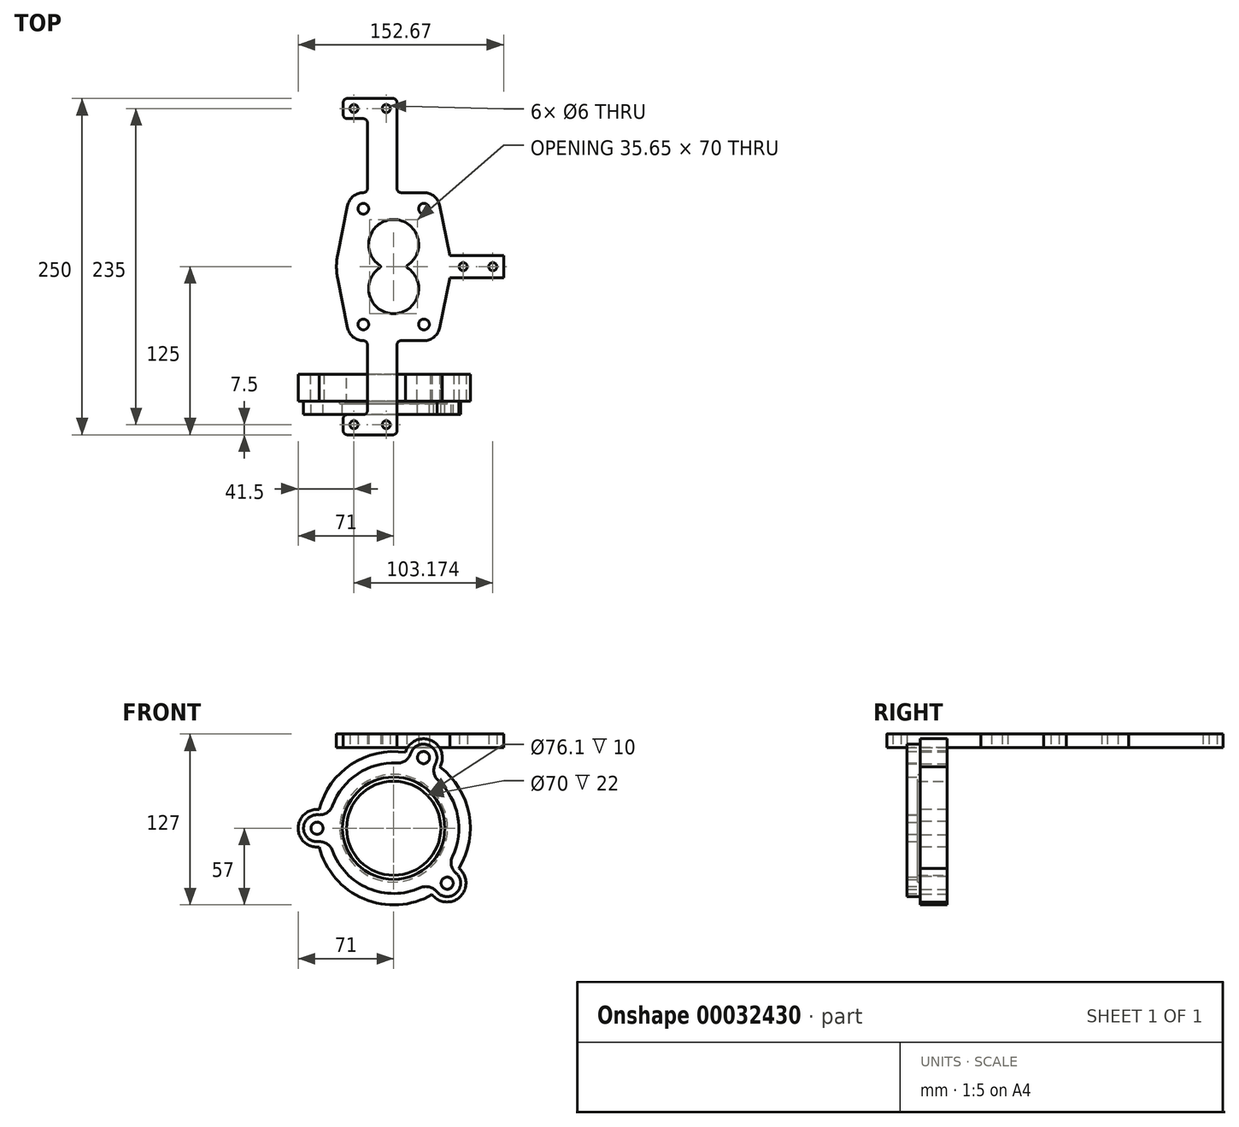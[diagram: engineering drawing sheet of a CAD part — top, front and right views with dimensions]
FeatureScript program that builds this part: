
annotation { "Feature Type Name" : "Feature", "Feature Type Description" : "" }
export const myFeature = defineFeature(function(context is Context, id is Id, definition is map)
    precondition{}
    {
        {
            var Q0;
            Q0=qCreatedBy(makeId("Front.planeOp"),FACE);
            var sketch = newSketch(context, id + "F0", { "sketchPlane" : qUnion([Q0])});
            skCircle(sketch, "E0", {"center": v(0, 0) * mm, "radius": 35 * mm});
            skCircle(sketch, "E1", {"center": v(0, 0) * mm, "radius": 40 * mm, "construction": true});
            skLineSegment(sketch, "E2", {"start": v(22.17, 52.51) * mm, "end": v(-57, 0) * mm, "construction": true});
            skLineSegment(sketch, "E3", {"start": v(39.76, -40.84) * mm, "end": v(22.17, 52.51) * mm, "construction": true});
            skLineSegment(sketch, "E4", {"start": v(-57, 0) * mm, "end": v(39.76, -40.84) * mm, "construction": true});
            skCircle(sketch, "E5", {"center": v(39.76, -40.84) * mm, "radius": 5 * mm});
            skCircle(sketch, "E6", {"center": v(22.17, 52.51) * mm, "radius": 5 * mm});
            skCircle(sketch, "E7", {"center": v(-57, 0) * mm, "radius": 5 * mm});
            skArc(sketch, "E8", {"start": v(34.3, 45.53) * mm, "mid": v(27.61, 65.41) * mm, "end": v(8.7, 56.33) * mm});
            skArc(sketch, "E9", {"start": v(28.6, -49.3) * mm, "mid": v(49.52, -50.88) * mm, "end": v(48.52, -29.92) * mm});
            skArc(sketch, "E10", {"start": v(-55.28, 13.9) * mm, "mid": v(-71, 0) * mm, "end": v(-55.28, -13.9) * mm});
            skArc(sketch, "E11.trimOffspring", {"start": v(8.7, 56.33) * mm, "mid": v(-31.5, 47.5) * mm, "end": v(-55.28, 13.9) * mm});
            skArc(sketch, "E12.trimOffspring", {"start": v(48.52, -29.92) * mm, "mid": v(56.01, 10.56) * mm, "end": v(34.3, 45.53) * mm});
            skArc(sketch, "E13.trimOffspring", {"start": v(-55.28, -13.9) * mm, "mid": v(-22.17, -52.51) * mm, "end": v(28.6, -49.3) * mm});
            skCircle(sketch, "E14", {"center": v(0, 0) * mm, "radius": 57 * mm, "construction": true});
            skSolve(sketch);
        }
        {
            var Q0;
            Q0=qCreatedBy(makeId("Top.planeOp"),FACE);
            cPlane(context, id + "F1", {"entities" : qUnion([Q0]), "cplaneType" : CPlaneType.OFFSET, "offset" : 60 * mm, "width" : 150 * mm, "height" : 150 * mm});
        }
        {
            var Q0;
            Q0=qCreatedBy(id+"F1.planeOp",FACE);
            var sketch = newSketch(context, id + "F2", { "sketchPlane" : qUnion([Q0])});
            skLineSegment(sketch, "E15.rect.bottom", {"start": v(22.5, 143) * mm, "end": v(-22.5, 143) * mm, "construction": true});
            skLineSegment(sketch, "E15.rect.top", {"start": v(22.5, 57) * mm, "end": v(-22.5, 57) * mm, "construction": true});
            skLineSegment(sketch, "E15.rect.left", {"start": v(22.5, 143) * mm, "end": v(22.5, 57) * mm, "construction": true});
            skLineSegment(sketch, "E15.rect.right", {"start": v(-22.5, 143) * mm, "end": v(-22.5, 57) * mm, "construction": true});
            skPoint(sketch, "E15.rect.middle", {"position": v(0, 100) * mm});
            skCircle(sketch, "E16", {"center": v(-22.5, 143) * mm, "radius": 4 * mm});
            skCircle(sketch, "E17", {"center": v(22.5, 143) * mm, "radius": 4 * mm});
            skCircle(sketch, "E18", {"center": v(22.5, 57) * mm, "radius": 4 * mm});
            skCircle(sketch, "E19", {"center": v(-22.5, 57) * mm, "radius": 4 * mm});
            skArc(sketch, "E20", {"start": v(-41.67, 108.34) * mm, "mid": v(-42.5, 100) * mm, "end": v(-41.67, 91.66) * mm});
            skArc(sketch, "E21", {"start": v(-22.5, 155) * mm, "mid": v(-30.1, 152.28) * mm, "end": v(-34.27, 145.35) * mm});
            skLineSegment(sketch, "E22", {"start": v(-34.27, 54.65) * mm, "end": v(-41.67, 91.66) * mm});
            skLineSegment(sketch, "E23", {"start": v(-34.27, 145.35) * mm, "end": v(-41.67, 108.34) * mm});
            skLineSegment(sketch, "E24", {"start": v(0, 155) * mm, "end": v(0, 45) * mm, "construction": true});
            skLineSegment(sketch, "E25", {"start": v(0, 45) * mm, "end": v(-22.5, 45) * mm, "construction": true});
            skArc(sketch, "E26.trimOffspring", {"start": v(-34.27, 54.65) * mm, "mid": v(-30.1, 47.72) * mm, "end": v(-22.5, 45) * mm});
            skLineSegment(sketch, "E27.MirrorCS", {"start": v(5.5, 155) * mm, "end": v(22.5, 155) * mm});
            skArc(sketch, "E28.MirrorCS", {"start": v(22.5, 155) * mm, "mid": v(30.1, 152.28) * mm, "end": v(34.27, 145.35) * mm});
            skLineSegment(sketch, "E29.MirrorCS", {"start": v(34.27, 145.35) * mm, "end": v(41.67, 108.34) * mm});
            skArc(sketch, "E30.MirrorCS", {"start": v(41.67, 108.34) * mm, "mid": v(42.5, 100) * mm, "end": v(41.67, 91.66) * mm, "construction": true});
            skLineSegment(sketch, "E31.MirrorCS", {"start": v(34.27, 54.65) * mm, "end": v(41.67, 91.66) * mm});
            skArc(sketch, "E32.MirrorCS", {"start": v(34.27, 54.65) * mm, "mid": v(30.1, 47.72) * mm, "end": v(22.5, 45) * mm});
            skLineSegment(sketch, "E33.MirrorCS", {"start": v(5.5, 45) * mm, "end": v(22.5, 45) * mm});
            skPoint(sketch, "E34.rect.bottom.start.orphan", {"position": v(0, 155) * mm});
            skLineSegment(sketch, "E35", {"start": v(41.67, 108.34) * mm, "end": v(81.67, 108.34) * mm});
            skLineSegment(sketch, "E36", {"start": v(81.67, 108.34) * mm, "end": v(81.67, 91.66) * mm});
            skLineSegment(sketch, "E37", {"start": v(81.67, 91.66) * mm, "end": v(41.67, 91.66) * mm});
            skArc(sketch, "E38.filletArc", {"start": v(-22.5, 155) * mm, "mid": v(-20.38, 155.88) * mm, "end": v(-19.5, 158) * mm});
            skArc(sketch, "E39.filletArc", {"start": v(2.5, 158) * mm, "mid": v(3.38, 155.88) * mm, "end": v(5.5, 155) * mm});
            skLineSegment(sketch, "E40", {"start": v(-19.5, 158) * mm, "end": v(-19.5, 207) * mm});
            skLineSegment(sketch, "E41", {"start": v(-22.5, 210) * mm, "end": v(-34.5, 210) * mm});
            skLineSegment(sketch, "E42", {"start": v(-37.5, 213) * mm, "end": v(-37.5, 222) * mm});
            skLineSegment(sketch, "E43", {"start": v(-34.5, 225) * mm, "end": v(-0.5, 225) * mm});
            skLineSegment(sketch, "E44", {"start": v(2.5, 222) * mm, "end": v(2.5, 158) * mm});
            skCircle(sketch, "E45", {"center": v(-29.5, 217.5) * mm, "radius": 3 * mm});
            skCircle(sketch, "E46", {"center": v(-5.5, 217.5) * mm, "radius": 3 * mm});
            skLineSegment(sketch, "E47", {"start": v(-29.5, 217.5) * mm, "end": v(-5.5, 217.5) * mm, "construction": true});
            skPoint(sketch, "E48.visualSharp", {"position": v(-37.5, 225) * mm});
            skArc(sketch, "E48.filletArc", {"start": v(-34.5, 225) * mm, "mid": v(-36.62, 224.12) * mm, "end": v(-37.5, 222) * mm});
            skPoint(sketch, "E49.visualSharp", {"position": v(2.5, 225) * mm});
            skArc(sketch, "E49.filletArc", {"start": v(2.5, 222) * mm, "mid": v(1.62, 224.12) * mm, "end": v(-0.5, 225) * mm});
            skPoint(sketch, "E50.visualSharp", {"position": v(-19.5, 210) * mm});
            skArc(sketch, "E50.filletArc", {"start": v(-19.5, 207) * mm, "mid": v(-20.38, 209.12) * mm, "end": v(-22.5, 210) * mm});
            skPoint(sketch, "E51.visualSharp", {"position": v(-37.5, 210) * mm});
            skArc(sketch, "E51.filletArc", {"start": v(-37.5, 213) * mm, "mid": v(-36.62, 210.88) * mm, "end": v(-34.5, 210) * mm});
            skLineSegment(sketch, "E52", {"start": v(0, 100) * mm, "end": v(-77.55, 100) * mm, "construction": true});
            skLineSegment(sketch, "E53", {"start": v(81.67, 100) * mm, "end": v(51.67, 100) * mm, "construction": true});
            skCircle(sketch, "E54", {"center": v(51.67, 100) * mm, "radius": 3 * mm});
            skCircle(sketch, "E55", {"center": v(73.67, 100) * mm, "radius": 3 * mm});
            skArc(sketch, "E56.MirrorCS", {"start": v(-37.5, -13) * mm, "mid": v(-36.62, -10.88) * mm, "end": v(-34.5, -10) * mm});
            skArc(sketch, "E57.MirrorCS", {"start": v(2.5, -22) * mm, "mid": v(1.62, -24.12) * mm, "end": v(-0.5, -25) * mm});
            skArc(sketch, "E58.MirrorCS", {"start": v(-19.5, -7) * mm, "mid": v(-20.38, -9.12) * mm, "end": v(-22.5, -10) * mm});
            skArc(sketch, "E59.MirrorCS", {"start": v(-34.5, -25) * mm, "mid": v(-36.62, -24.12) * mm, "end": v(-37.5, -22) * mm});
            skPoint(sketch, "E60.MirrorP", {"position": v(-37.5, -25) * mm});
            skLineSegment(sketch, "E61.MirrorCS", {"start": v(-29.5, -17.5) * mm, "end": v(-5.5, -17.5) * mm});
            skLineSegment(sketch, "E62.MirrorCS", {"start": v(-22.5, -10) * mm, "end": v(-34.5, -10) * mm});
            skPoint(sketch, "E63.MirrorP", {"position": v(-19.5, -10) * mm});
            skLineSegment(sketch, "E64.MirrorCS", {"start": v(2.5, -22) * mm, "end": v(2.5, 42) * mm});
            skPoint(sketch, "E65.MirrorP", {"position": v(2.5, -25) * mm});
            skCircle(sketch, "E66.MirrorC", {"center": v(-29.5, -17.5) * mm, "radius": 3 * mm});
            skPoint(sketch, "E67.MirrorP", {"position": v(-37.5, -10) * mm});
            skLineSegment(sketch, "E68.MirrorCS", {"start": v(-37.5, -13) * mm, "end": v(-37.5, -22) * mm});
            skLineSegment(sketch, "E69.MirrorCS", {"start": v(-19.5, 42) * mm, "end": v(-19.5, -7) * mm});
            skLineSegment(sketch, "E70.MirrorCS", {"start": v(-34.5, -25) * mm, "end": v(-0.5, -25) * mm});
            skCircle(sketch, "E71.MirrorC", {"center": v(-5.5, -17.5) * mm, "radius": 3 * mm});
            skArc(sketch, "E72.MirrorCS", {"start": v(-22.5, 45) * mm, "mid": v(-20.38, 44.12) * mm, "end": v(-19.5, 42) * mm});
            skArc(sketch, "E73.MirrorCS", {"start": v(2.5, 42) * mm, "mid": v(3.38, 44.12) * mm, "end": v(5.5, 45) * mm});
            skPoint(sketch, "E74.orphan", {"position": v(0, 45) * mm});
            skArc(sketch, "E75", {"start": v(-8.77, 100) * mm, "mid": v(0, 65) * mm, "end": v(8.77, 100) * mm});
            skLineSegment(sketch, "E76", {"start": v(0, 100) * mm, "end": v(0, 100) * mm});
            skCircle(sketch, "E77", {"center": v(0, 100) * mm, "radius": 35 * mm, "construction": true});
            skPoint(sketch, "E78", {"position": v(22.5, 100) * mm});
            skArc(sketch, "E79.converted", {"start": v(8.77, 100) * mm, "mid": v(0, 135) * mm, "end": v(-8.77, 100) * mm});
            skSolve(sketch);
        }
        {
            var Q0;
            Q0=qCreatedBy(makeId("Right.planeOp"),FACE);
            var sketch = newSketch(context, id + "F3", { "sketchPlane" : qUnion([Q0])});
            skLineSegment(sketch, "E80", {"start": v(0, 0) * mm, "end": v(19.92, 0) * mm});
            skSolve(sketch);
        }
        {
            var Q0;
            Q0=sQuery(id+"F3.wireOp",EDGE,"E80");
            cPlane(context, id + "F4", {"entities" : qUnion([Q0]), "cplaneType" : CPlaneType.LINE_ANGLE, "offset" : 150 * mm, "angle" : 65 * degree, "width" : 150 * mm, "height" : 150 * mm});
        }
        {
            var Q0;
            Q0=qCreatedBy(id+"F4.planeOp",FACE);
            var sketch = newSketch(context, id + "F5", { "sketchPlane" : qUnion([Q0])});
            skLineSegment(sketch, "E81", {"start": v(35.53, 0) * mm, "end": v(0, 0) * mm, "construction": true});
            skArc(sketch, "E82", {"start": v(0, 0) * mm, "mid": v(-23.3, -3.07) * mm, "end": v(-45, -12.06) * mm});
            skLineSegment(sketch, "E83", {"start": v(-45, -12.06) * mm, "end": v(0, -90) * mm, "construction": true});
            skLineSegment(sketch, "E84", {"start": v(0, 0) * mm, "end": v(0, -90) * mm, "construction": true});
            skSolve(sketch);
        }
        {
            var Q0;
            Q0=makeQuery(id+"F0.imprint","IMPRINT",FACE,{"disambiguationData":[TD([[makeQuery(id+"F0.imprint","IMPRINT",EDGE,{"derivedFrom":sQuery(id+"F0.wireOp",EDGE,"E0")}),-1.0]])]});
            var sketch = newSketch(context, id + "F6", { "sketchPlane" : qUnion([Q0])});
            skCircle(sketch, "E85", {"center": v(0, 0) * mm, "radius": 40 * mm});
            skSolve(sketch);
        }
        {
            var Q0;
            Q0=makeQuery(id+"F6.imprint","IMPRINT",FACE,{"disambiguationData":[TD([[makeQuery(id+"F6.imprint","IMPRINT",EDGE,{"derivedFrom":sQuery(id+"F6.wireOp",EDGE,"E85")}),1.0]])]});
            extrude(context, id + "F7", {"entities" : qUnion([Q0]), "depth" : 2 * mm});
        }
        {
            var Q0;
            Q0=makeQuery(id+"F0.imprint","IMPRINT",FACE,{"disambiguationData":[TD([[makeQuery(id+"F0.imprint","IMPRINT",EDGE,{"derivedFrom":sQuery(id+"F0.wireOp",EDGE,"E0")}),-1.0]])]});
            extrude(context, id + "F8", {"entities" : qUnion([Q0]), "operationType" : NewBodyOperationType.ADD, "oppositeDirection" : true, "depth" : 20 * mm});
        }
        {
            var Q0;
            Q0 = qSketchRegion(id + "F2", true);
            extrude(context, id + "F9", {"entities" : qUnion([Q0]), "depth" : 10 * mm});
        }
        {
            var Q0;
            Q0=makeQuery(id+"F8.opExtrude","CAP_FACE",FACE,{"disambiguationData":[OSD([sQuery(id+"F0.wireOp",EDGE,"E0"),sQuery(id+"F0.wireOp",EDGE,"E5"),sQuery(id+"F0.wireOp",EDGE,"E6"),sQuery(id+"F0.wireOp",EDGE,"E7"),sQuery(id+"F0.wireOp",EDGE,"E8"),sQuery(id+"F0.wireOp",EDGE,"E9"),sQuery(id+"F0.wireOp",EDGE,"E10"),sQuery(id+"F0.wireOp",EDGE,"E11.trimOffspring"),sQuery(id+"F0.wireOp",EDGE,"E12.trimOffspring"),sQuery(id+"F0.wireOp",EDGE,"E13.trimOffspring")])],"isStart":true});
            var sketch = newSketch(context, id + "F10", { "sketchPlane" : qUnion([Q0])});
            skCircle(sketch, "E86.0", {"center": v(39.76, -40.84) * mm, "radius": 4.5 * mm});
            skCircle(sketch, "E86.1", {"center": v(22.17, 52.51) * mm, "radius": 4.5 * mm});
            skCircle(sketch, "E86.2", {"center": v(-57, 0) * mm, "radius": 4.5 * mm});
            skCircle(sketch, "E87.0", {"center": v(0, 0) * mm, "radius": 38.05 * mm});
            skArc(sketch, "E88", {"start": v(43.72, -21) * mm, "mid": v(47.66, 8.98) * mm, "end": v(33.08, 35.47) * mm});
            skCircle(sketch, "E89", {"center": v(0, 0) * mm, "radius": 57 * mm, "construction": true});
            skArc(sketch, "E90", {"start": v(32, -47.16) * mm, "mid": v(46.73, -48) * mm, "end": v(46.29, -33.27) * mm});
            skLineSegment(sketch, "E91", {"start": v(32, -47.16) * mm, "end": v(19.81, -44.27) * mm, "construction": true});
            skLineSegment(sketch, "E92", {"start": v(46.29, -33.27) * mm, "end": v(43.72, -21) * mm, "construction": true});
            skLineSegment(sketch, "E93", {"start": v(0, 0) * mm, "end": v(39.76, -40.84) * mm, "construction": true});
            skLineSegment(sketch, "E94", {"start": v(0, 0) * mm, "end": v(-57, 0) * mm, "construction": true});
            skLineSegment(sketch, "E95", {"start": v(0, 0) * mm, "end": v(22.17, 52.51) * mm, "construction": true});
            skArc(sketch, "E96", {"start": v(43.72, -21) * mm, "mid": v(42.92, -27.57) * mm, "end": v(46.29, -33.27) * mm});
            skArc(sketch, "E97", {"start": v(32, -47.16) * mm, "mid": v(26.4, -43.65) * mm, "end": v(19.81, -44.27) * mm});
            skArc(sketch, "E98", {"start": v(-56.12, 9.96) * mm, "mid": v(-67, 0) * mm, "end": v(-56.12, -9.96) * mm});
            skArc(sketch, "E99.trimOffspring", {"start": v(-45.54, -16.68) * mm, "mid": v(-18.86, -44.68) * mm, "end": v(19.81, -44.27) * mm});
            skArc(sketch, "E100", {"start": v(-56.12, 9.96) * mm, "mid": v(-49.7, 11.53) * mm, "end": v(-45.54, 16.68) * mm});
            skArc(sketch, "E101", {"start": v(-45.54, -16.68) * mm, "mid": v(-49.7, -11.53) * mm, "end": v(-56.12, -9.96) * mm});
            skArc(sketch, "E102", {"start": v(31, 47.83) * mm, "mid": v(26.06, 61.73) * mm, "end": v(12.65, 55.58) * mm});
            skArc(sketch, "E103.trimOffspring", {"start": v(2.34, 48.44) * mm, "mid": v(-26.8, 40.42) * mm, "end": v(-45.54, 16.68) * mm});
            skArc(sketch, "E104", {"start": v(2.34, 48.44) * mm, "mid": v(8.7, 50.26) * mm, "end": v(12.65, 55.58) * mm});
            skArc(sketch, "E105", {"start": v(31, 47.83) * mm, "mid": v(29.95, 41.3) * mm, "end": v(33.08, 35.47) * mm});
            skSolve(sketch);
        }
        {
            var Q0;
            Q0 = qSketchRegion(id + "F10", true);
            extrude(context, id + "F11", {"entities" : qUnion([Q0]), "depth" : 10 * mm});
        }
        {
            var Q0;
            {var subQ0=sQuery(id+"F2.wireOp",EDGE,"E75");var subQ1=sQuery(id+"F2.wireOp",EDGE,"E79.converted");Q0=makeQuery(id+"F9.opExtrude","SWEPT_EDGE",EDGE,{"disambiguationData":[OSD([subQ0,subQ1]),TDD([makeQuery(id+"F2.imprint","INTERSECT",VERTEX,{"disambiguationData":[OD(1.0)],"derivedFrom":[subQ0,subQ1]})])]});}
            var Q1;
            {var subQ0=sQuery(id+"F2.wireOp",EDGE,"E75");var subQ1=sQuery(id+"F2.wireOp",EDGE,"E79.converted");Q1=makeQuery(id+"F9.opExtrude","SWEPT_EDGE",EDGE,{"disambiguationData":[OSD([subQ0,subQ1]),TDD([makeQuery(id+"F2.imprint","INTERSECT",VERTEX,{"disambiguationData":[OD(0.0)],"derivedFrom":[subQ0,subQ1]})])]});}
            fillet(context, id + "F12", {"entities" : qUnion([Q0, Q1]), "radius" : 1 * mm, "tangentPropagation" : true, "allowEdgeOverflow" : false});
        }
    });
